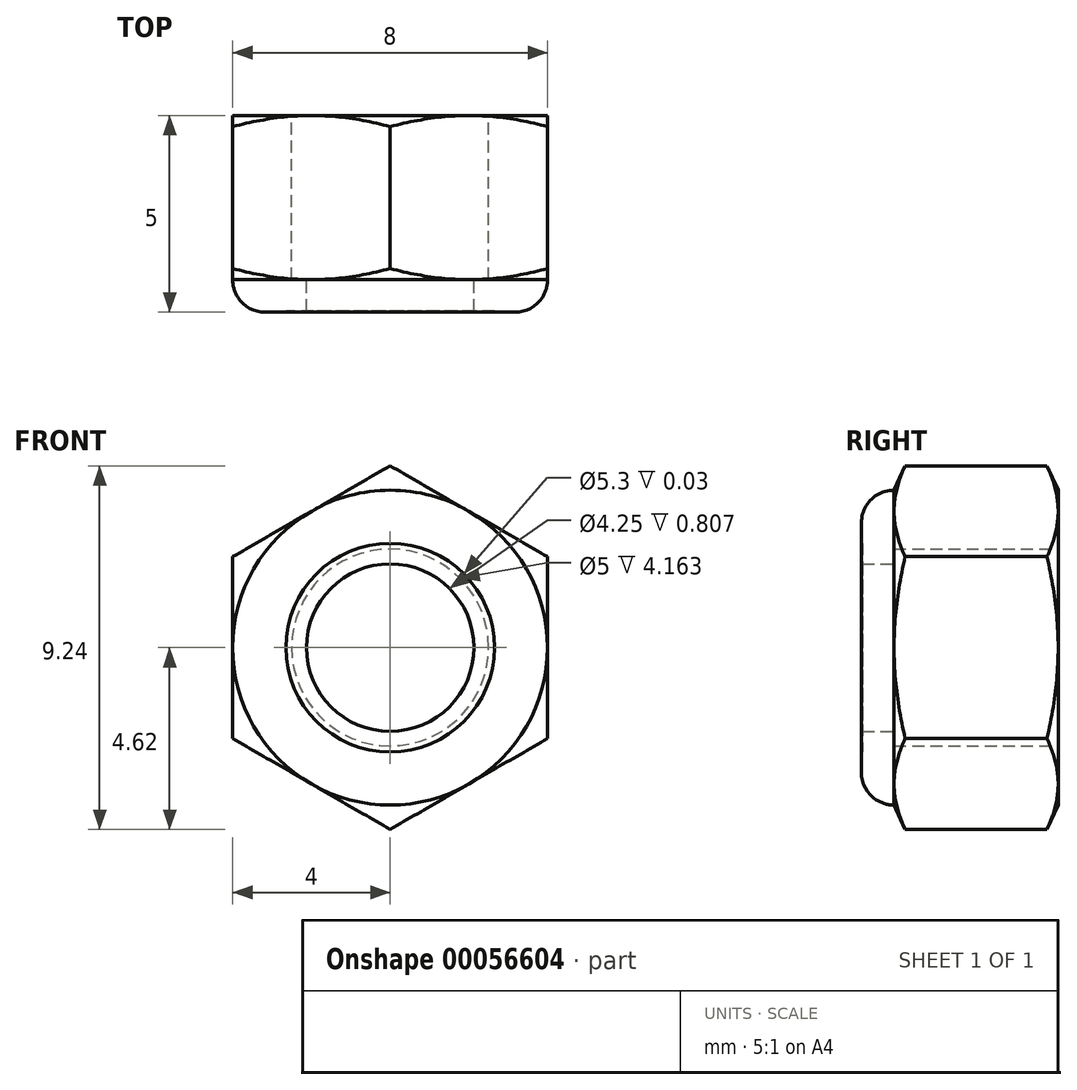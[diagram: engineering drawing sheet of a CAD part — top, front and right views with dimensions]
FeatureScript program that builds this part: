
annotation { "Feature Type Name" : "Feature", "Feature Type Description" : "" }
export const myFeature = defineFeature(function(context is Context, id is Id, definition is map)
    precondition{}
    {
        {
            var Q0;
            Q0=qCreatedBy(makeId("Right.planeOp"),FACE);
            var sketch = newSketch(context, id + "F0", { "sketchPlane" : qUnion([Q0])});
            skLineSegment(sketch, "E0", {"start": v(0, 0) * mm, "end": v(19.01, 0) * mm, "construction": true});
            skLineSegment(sketch, "E1", {"start": v(0, 6.95) * mm, "end": v(0.5, 6.95) * mm});
            skLineSegment(sketch, "E2", {"start": v(0.5, 6.95) * mm, "end": v(0.5, 7.99) * mm});
            skLineSegment(sketch, "E3", {"start": v(0.5, 7.99) * mm, "end": v(5.1, 7.99) * mm});
            skLineSegment(sketch, "E4", {"start": v(5.1, 7.99) * mm, "end": v(5.1, 9.8) * mm});
            skLineSegment(sketch, "E5", {"start": v(5.1, 9.8) * mm, "end": v(2.95, 11.96) * mm});
            skLineSegment(sketch, "E6", {"start": v(2.95, 11.96) * mm, "end": v(0, 11.96) * mm});
            skLineSegment(sketch, "E7", {"start": v(0, 0) * mm, "end": v(0, 11.96) * mm, "construction": true});
            skLineSegment(sketch, "E8.MirrorCS", {"start": v(0, 6.95) * mm, "end": v(-0.5, 6.95) * mm});
            skLineSegment(sketch, "E9.MirrorCS", {"start": v(-2.95, 11.96) * mm, "end": v(0, 11.96) * mm});
            skLineSegment(sketch, "E10.MirrorCS", {"start": v(-0.5, 6.95) * mm, "end": v(-0.5, 7.99) * mm});
            skLineSegment(sketch, "E11.MirrorCS", {"start": v(-5.1, 7.99) * mm, "end": v(-5.1, 9.8) * mm});
            skLineSegment(sketch, "E12.MirrorCS", {"start": v(-0.5, 7.99) * mm, "end": v(-5.1, 7.99) * mm});
            skLineSegment(sketch, "E13.MirrorCS", {"start": v(-5.1, 9.8) * mm, "end": v(-2.95, 11.96) * mm});
            skSolve(sketch);
        }
        {
            var Q0;
            Q0 = qSketchRegion(id + "F0", true);
            var Q1;
            Q1=sQuery(id+"F0.wireOp",EDGE,"E0");
            revolve(context, id + "F1", {"entities" : qUnion([Q0]), "axis" : qUnion([Q1]), "revolveType" : RevolveType.FULL});
        }
        {
            var Q0;
            Q0=qCreatedBy(makeId("Front.planeOp"),FACE);
            var sketch = newSketch(context, id + "F2", { "sketchPlane" : qUnion([Q0])});
            skCircle(sketch, "E14", {"center": v(0, 0) * mm, "radius": 5 * mm});
            skCircle(sketch, "E15", {"center": v(0, 0) * mm, "radius": 2.5 * mm});
            skSolve(sketch);
        }
        {
            var Q0;
            Q0 = qSketchRegion(id + "F2", true);
            extrude(context, id + "F3", {"entities" : qUnion([Q0]), "depth" : 1 * mm, "symmetric" : true});
        }
        {
            var Q0;
            Q0=qCreatedBy(makeId("Right.planeOp"),FACE);
            var sketch = newSketch(context, id + "F4", { "sketchPlane" : qUnion([Q0])});
            skLineSegment(sketch, "E16.0.0", {"start": v(-0.5, -5) * mm, "end": v(-0.5, 5) * mm, "construction": true});
            skLineSegment(sketch, "E17", {"start": v(-0.5, 2.5) * mm, "end": v(-5.5, 2.5) * mm});
            skLineSegment(sketch, "E18.MirrorCS", {"start": v(-0.5, 2.5) * mm, "end": v(-0.5, 4.3) * mm});
            skLineSegment(sketch, "E19.MirrorCS", {"start": v(-0.5, 4.3) * mm, "end": v(-0.8, 4.3) * mm});
            skLineSegment(sketch, "E20.MirrorCS", {"start": v(-0.8, 4.3) * mm, "end": v(-0.8, 6.8) * mm});
            skLineSegment(sketch, "E21", {"start": v(-0.8, 6.8) * mm, "end": v(-0.5, 6.8) * mm});
            skLineSegment(sketch, "E22", {"start": v(-0.5, 6.8) * mm, "end": v(-0.5, 8) * mm});
            skLineSegment(sketch, "E23", {"start": v(-0.5, 8) * mm, "end": v(-5.5, 8) * mm});
            skLineSegment(sketch, "E24", {"start": v(-3, 8) * mm, "end": v(-3, 2.5) * mm, "construction": true});
            skLineSegment(sketch, "E25.MirrorCS", {"start": v(-5.5, 6.8) * mm, "end": v(-5.5, 8) * mm});
            skLineSegment(sketch, "E26.MirrorCS", {"start": v(-5.5, 2.5) * mm, "end": v(-5.5, 4.3) * mm});
            skLineSegment(sketch, "E27.MirrorCS", {"start": v(-5.2, 4.3) * mm, "end": v(-5.2, 6.8) * mm});
            skLineSegment(sketch, "E28.MirrorCS", {"start": v(-5.2, 6.8) * mm, "end": v(-5.5, 6.8) * mm});
            skLineSegment(sketch, "E29.MirrorCS", {"start": v(-5.5, 4.3) * mm, "end": v(-5.2, 4.3) * mm});
            skLineSegment(sketch, "E30", {"start": v(0, 0) * mm, "end": v(-5.5, 0) * mm, "construction": true});
            skSolve(sketch);
        }
        {
            var Q0;
            Q0 = qSketchRegion(id + "F4", true);
            var Q1;
            Q1=sQuery(id+"F4.wireOp",EDGE,"E30");
            revolve(context, id + "F5", {"entities" : qUnion([Q0]), "axis" : qUnion([Q1]), "revolveType" : RevolveType.FULL});
        }
        {
            var Q0;
            Q0=makeQuery(id+"F5.opRevolve","SWEPT_EDGE",EDGE,{"disambiguationData":[OSD([sQuery(id+"F4.wireOp",EDGE,"E23"),sQuery(id+"F4.wireOp",EDGE,"E25.MirrorCS")])]});
            var Q1;
            Q1=makeQuery(id+"F5.opRevolve","SWEPT_EDGE",EDGE,{"disambiguationData":[OSD([sQuery(id+"F4.wireOp",EDGE,"E22"),sQuery(id+"F4.wireOp",EDGE,"E23")])]});
            var Q2;
            Q2=makeQuery(id+"F5.opRevolve","SWEPT_EDGE",EDGE,{"disambiguationData":[OSD([sQuery(id+"F4.wireOp",EDGE,"E17"),sQuery(id+"F4.wireOp",EDGE,"E26.MirrorCS")])]});
            var Q3;
            Q3=makeQuery(id+"F5.opRevolve","SWEPT_EDGE",EDGE,{"disambiguationData":[OSD([sQuery(id+"F4.wireOp",EDGE,"E17"),sQuery(id+"F4.wireOp",EDGE,"E18.MirrorCS")])]});
            chamfer(context, id + "F6", {"entities" : qUnion([Q0, Q1, Q2, Q3]), "width" : 0.25 * mm, "tangentPropagation" : true});
        }
        {
            var Q0;
            Q0=qCreatedBy(makeId("Right.planeOp"),FACE);
            var sketch = newSketch(context, id + "F7", { "sketchPlane" : qUnion([Q0])});
            skLineSegment(sketch, "E31.0.0", {"start": v(-5.5, -4.3) * mm, "end": v(-5.5, 4.3) * mm, "construction": true});
            skLineSegment(sketch, "E32", {"start": v(-7.59, 8.6) * mm, "end": v(-7.59, -8) * mm, "construction": true});
            skLineSegment(sketch, "E33", {"start": v(-5.5, 4) * mm, "end": v(-5.79, 4.62) * mm});
            skLineSegment(sketch, "E34", {"start": v(-5.79, 4.62) * mm, "end": v(-7.59, 4.62) * mm});
            skLineSegment(sketch, "E35.MirrorCS", {"start": v(-9.39, 4.62) * mm, "end": v(-7.59, 4.62) * mm});
            skLineSegment(sketch, "E36.MirrorCS", {"start": v(-9.67, 4) * mm, "end": v(-9.39, 4.62) * mm});
            skLineSegment(sketch, "E37", {"start": v(-5.5, 0) * mm, "end": v(0, 0) * mm, "construction": true});
            skLineSegment(sketch, "E38", {"start": v(-5.5, 2.5) * mm, "end": v(-5.5, 4) * mm});
            skLineSegment(sketch, "E39", {"start": v(-5.5, 0) * mm, "end": v(-10.5, 0) * mm, "construction": true});
            skArc(sketch, "E40", {"start": v(-9.67, 4) * mm, "mid": v(-10.26, 3.76) * mm, "end": v(-10.5, 3.17) * mm});
            skLineSegment(sketch, "E41", {"start": v(-5.5, 2.5) * mm, "end": v(-9.66, 2.5) * mm});
            skLineSegment(sketch, "E42", {"start": v(-9.66, 2.5) * mm, "end": v(-9.66, 2.13) * mm});
            skLineSegment(sketch, "E43", {"start": v(-9.66, 2.13) * mm, "end": v(-10.47, 2.13) * mm});
            skLineSegment(sketch, "E44", {"start": v(-10.47, 2.13) * mm, "end": v(-10.47, 2.65) * mm});
            skLineSegment(sketch, "E45", {"start": v(-10.47, 2.65) * mm, "end": v(-10.5, 2.65) * mm});
            skLineSegment(sketch, "E46", {"start": v(-10.5, 2.65) * mm, "end": v(-10.5, 3.17) * mm});
            skLineSegment(sketch, "E47", {"start": v(-9.67, 4) * mm, "end": v(-5.5, 4) * mm, "construction": true});
            skSolve(sketch);
        }
        {
            var Q0;
            Q0 = qSketchRegion(id + "F7", true);
            var Q1;
            Q1=sQuery(id+"F7.wireOp",EDGE,"E39");
            revolve(context, id + "F8", {"entities" : qUnion([Q0]), "axis" : qUnion([Q1]), "revolveType" : RevolveType.FULL});
        }
        {
            var Q0;
            Q0=makeQuery(id+"F8.opRevolve","SWEPT_FACE",FACE,{"disambiguationData":[OSD([sQuery(id+"F7.wireOp",EDGE,"E38")])]});
            var sketch = newSketch(context, id + "F9", { "sketchPlane" : qUnion([Q0])});
            skCircle(sketch, "E48.cCircle", {"center": v(0, 0) * mm, "radius": 4 * mm, "construction": true});
            skLineSegment(sketch, "E48.0", {"start": v(4, 2.3) * mm, "end": v(4, -2.3) * mm});
            skLineSegment(sketch, "E48.1", {"start": v(4, -2.3) * mm, "end": v(0, -4.62) * mm});
            skLineSegment(sketch, "E48.2", {"start": v(0, -4.62) * mm, "end": v(-4, -2.3) * mm});
            skLineSegment(sketch, "E48.3", {"start": v(-4, -2.3) * mm, "end": v(-4, 2.3) * mm});
            skLineSegment(sketch, "E48.4", {"start": v(-4, 2.3) * mm, "end": v(0, 4.62) * mm});
            skLineSegment(sketch, "E48.5", {"start": v(0, 4.62) * mm, "end": v(4, 2.3) * mm});
            skPoint(sketch, "E48.0.midPoint", {"position": v(4, 0) * mm});
            skSolve(sketch);
        }
        {
            var Q0;
            Q0 = qSketchRegion(id + "F9", true);
            extrude(context, id + "F10", {"entities" : qUnion([Q0]), "operationType" : NewBodyOperationType.INTERSECT, "endBound" : BoundingType.THROUGH_ALL, "oppositeDirection" : true, "depth" : 25 * mm});
        }
    });
